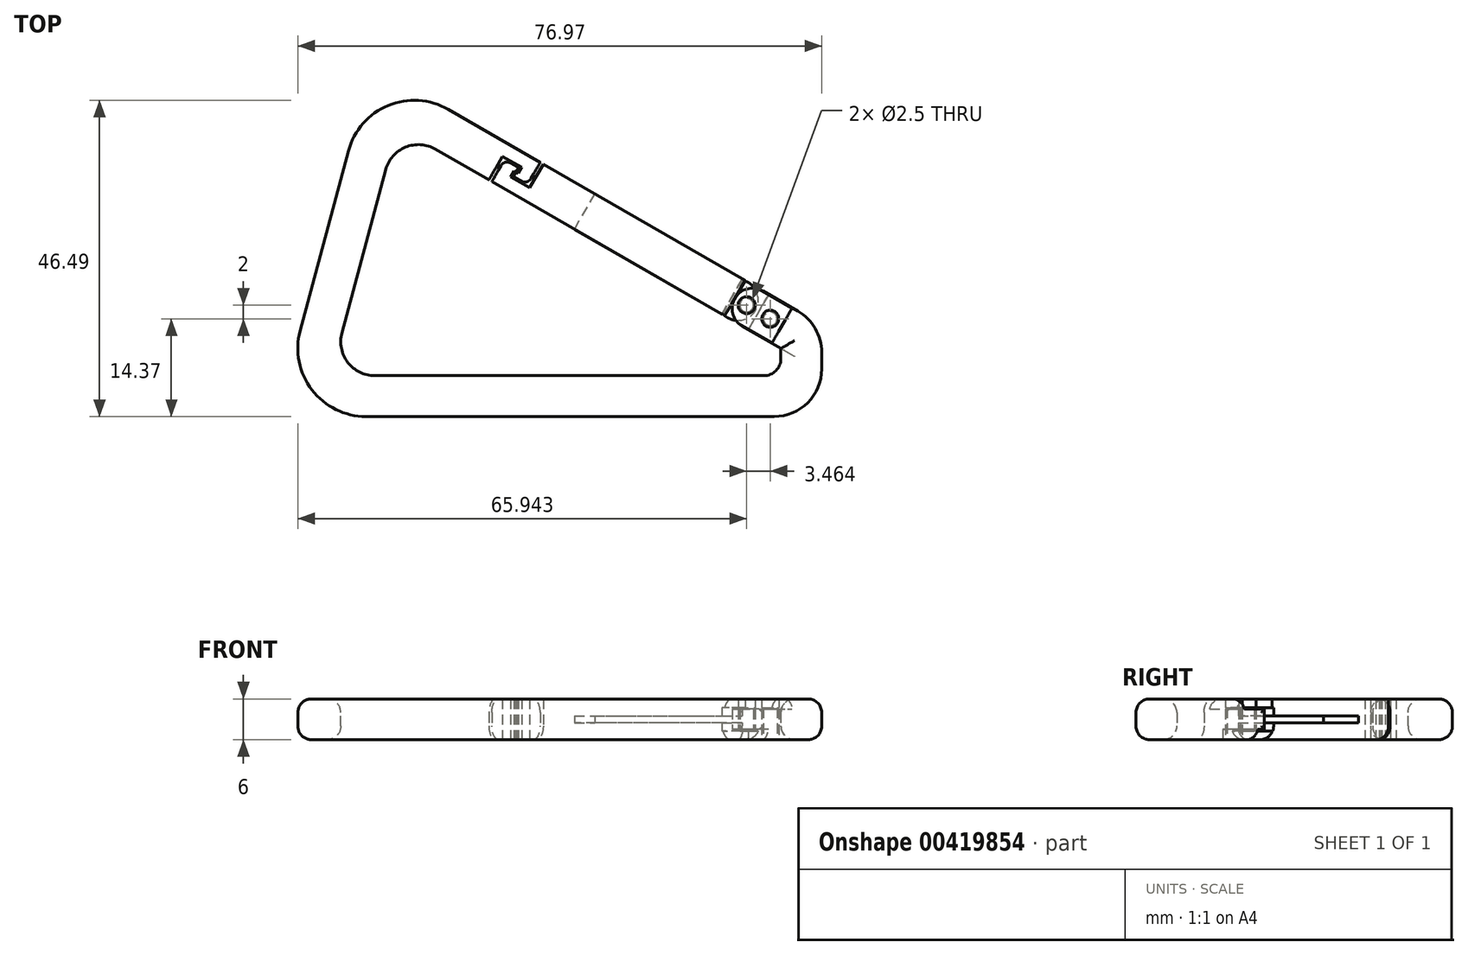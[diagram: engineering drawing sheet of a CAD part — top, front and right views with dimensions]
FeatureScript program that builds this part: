
annotation { "Feature Type Name" : "Feature", "Feature Type Description" : "" }
export const myFeature = defineFeature(function(context is Context, id is Id, definition is map)
    precondition{}
    {
        {
            var Q0;
            Q0=qCreatedBy(makeId("Top.planeOp"),FACE);
            var sketch = newSketch(context, id + "F0", { "sketchPlane" : qUnion([Q0])});
            skLineSegment(sketch, "E0", {"start": v(-46.88, -26.08) * mm, "end": v(33.12, -26.08) * mm});
            skLineSegment(sketch, "E1", {"start": v(33.12, -26.08) * mm, "end": v(33.12, -12.61) * mm});
            skLineSegment(sketch, "E2", {"start": v(33.12, -12.61) * mm, "end": v(21.86, -6.11) * mm});
            skLineSegment(sketch, "E3", {"start": v(-46.88, -26.08) * mm, "end": v(-33.04, 25.58) * mm});
            skLineSegment(sketch, "E4", {"start": v(-33.04, 25.58) * mm, "end": v(-12.78, 13.89) * mm});
            skLineSegment(sketch, "E5", {"start": v(-12.78, 13.89) * mm, "end": v(-15.78, 8.7) * mm});
            skLineSegment(sketch, "E6", {"start": v(-15.78, 8.7) * mm, "end": v(-29.27, 16.48) * mm});
            skLineSegment(sketch, "E7", {"start": v(-29.27, 16.48) * mm, "end": v(-39.06, -20.08) * mm});
            skLineSegment(sketch, "E8", {"start": v(-39.06, -20.08) * mm, "end": v(27.12, -20.08) * mm});
            skLineSegment(sketch, "E9", {"start": v(27.12, -20.08) * mm, "end": v(27.12, -20.08) * mm});
            skLineSegment(sketch, "E10", {"start": v(27.12, -20.08) * mm, "end": v(27.12, -16.08) * mm});
            skLineSegment(sketch, "E11", {"start": v(27.12, -16.08) * mm, "end": v(18.86, -11.3) * mm});
            skLineSegment(sketch, "E12", {"start": v(18.86, -11.3) * mm, "end": v(21.86, -6.11) * mm});
            skLineSegment(sketch, "E13", {"start": v(60.44, -26.08) * mm, "end": v(-63.58, 45.53) * mm, "construction": true});
            skLineSegment(sketch, "E14", {"start": v(-15.95, 15.72) * mm, "end": v(-8.23, 11.26) * mm});
            skLineSegment(sketch, "E15", {"start": v(-8.23, 11.26) * mm, "end": v(-10.1, 8.02) * mm});
            skLineSegment(sketch, "E16", {"start": v(-10.1, 8.02) * mm, "end": v(-11.84, 9.02) * mm});
            skLineSegment(sketch, "E17", {"start": v(-11.84, 9.02) * mm, "end": v(-11.84, 9.02) * mm});
            skLineSegment(sketch, "E18", {"start": v(-11.84, 9.02) * mm, "end": v(-10.97, 10.53) * mm});
            skLineSegment(sketch, "E19", {"start": v(-10.97, 10.53) * mm, "end": v(-13.78, 12.16) * mm});
            skLineSegment(sketch, "E20", {"start": v(-25.7, 17.88) * mm, "end": v(28.11, -13.19) * mm, "construction": true});
            skLineSegment(sketch, "E21", {"start": v(17.25, -10.38) * mm, "end": v(-15.35, 8.44) * mm});
            skLineSegment(sketch, "E22", {"start": v(-15.35, 8.44) * mm, "end": v(-13.47, 11.7) * mm});
            skLineSegment(sketch, "E23", {"start": v(-13.47, 11.7) * mm, "end": v(-13.47, 11.7) * mm});
            skLineSegment(sketch, "E24", {"start": v(-13.47, 11.7) * mm, "end": v(-11.74, 10.7) * mm});
            skLineSegment(sketch, "E25", {"start": v(-11.74, 10.7) * mm, "end": v(-12.62, 9.17) * mm});
            skLineSegment(sketch, "E26", {"start": v(-12.62, 9.17) * mm, "end": v(-9.8, 7.55) * mm});
            skLineSegment(sketch, "E27", {"start": v(-9.8, 7.55) * mm, "end": v(-7.8, 11.01) * mm});
            skLineSegment(sketch, "E28", {"start": v(-7.8, 11.01) * mm, "end": v(21.43, -5.86) * mm});
            skLineSegment(sketch, "E29", {"start": v(21.43, -5.86) * mm, "end": v(18.43, -11.06) * mm});
            skLineSegment(sketch, "E30", {"start": v(18.43, -11.06) * mm, "end": v(17.25, -10.38) * mm});
            skLineSegment(sketch, "E31", {"start": v(25.32, -8.11) * mm, "end": v(22.32, -13.3) * mm});
            skLineSegment(sketch, "E32", {"start": v(25.79, -15.3) * mm, "end": v(28.79, -10.11) * mm});
            skCircle(sketch, "E33", {"center": v(22.1, -9.7) * mm, "radius": 1.25 * mm});
            skCircle(sketch, "E34", {"center": v(25.56, -11.7) * mm, "radius": 1.25 * mm});
            skCircle(sketch, "E35", {"center": v(22.1, -9.7) * mm, "radius": 1 * mm});
            skCircle(sketch, "E36", {"center": v(25.56, -11.7) * mm, "radius": 1 * mm});
            skLineSegment(sketch, "E37", {"start": v(-11.81, 9.87) * mm, "end": v(-11.47, 9.67) * mm});
            skLineSegment(sketch, "E38", {"start": v(-11.74, 10.7) * mm, "end": v(-11.4, 10.5) * mm});
            skLineSegment(sketch, "E39", {"start": v(-11.4, 10.5) * mm, "end": v(-11.77, 9.84) * mm});
            skLineSegment(sketch, "E40", {"start": v(-11.77, 9.84) * mm, "end": v(-12.12, 10.04) * mm});
            skLineSegment(sketch, "E41", {"start": v(-11.84, 9.02) * mm, "end": v(-12.2, 9.22) * mm});
            skLineSegment(sketch, "E42", {"start": v(-12.2, 9.22) * mm, "end": v(-11.81, 9.87) * mm});
            skSolve(sketch);
        }
        {
            var Q0;
            Q0=makeQuery(id+"F0.imprint","IMPRINT",FACE,{"disambiguationData":[TD([[makeQuery(id+"F0.imprint","IMPRINT",EDGE,{"derivedFrom":sQuery(id+"F0.wireOp",EDGE,"E0")}),1.0]])]});
            var Q1;
            {var subQ1=sQuery(id+"F0.wireOp",EDGE,"E15");Q1=makeQuery(id+"F0.imprint","IMPRINT",FACE,{"disambiguationData":[TD([[makeQuery(id+"F0.imprint","IMPRINT",EDGE,{"derivedFrom":subQ1}),-1.0]])]});}
            var Q2;
            {var subQ1=sQuery(id+"F0.wireOp",EDGE,"E31");Q2=makeQuery(id+"F0.imprint","IMPRINT",FACE,{"disambiguationData":[TD([[makeQuery(id+"F0.imprint","IMPRINT",EDGE,{"derivedFrom":subQ1}),1.0]])]});}
            var Q3;
            {var subQ0=sQuery(id+"F0.wireOp",EDGE,"E12");Q3=makeQuery(id+"F0.imprint","IMPRINT",FACE,{"disambiguationData":[TD([[makeQuery(id+"F0.imprint","IMPRINT",EDGE,{"derivedFrom":subQ0}),-1.0]])]});}
            var Q4;
            {var subQ1=sQuery(id+"F0.wireOp",EDGE,"E37");Q4=makeQuery(id+"F0.imprint","IMPRINT",FACE,{"disambiguationData":[TD([[makeQuery(id+"F0.imprint","IMPRINT",EDGE,{"derivedFrom":subQ1}),-1.0]])]});}
            extrude(context, id + "F1", {"entities" : qUnion([Q0, Q1, Q2, Q3, Q4]), "depth" : 6 * mm});
        }
        {
            var Q0;
            Q0=makeQuery(id+"F1.opExtrude","SWEPT_EDGE",EDGE,{"disambiguationData":[OSD([sQuery(id+"F0.wireOp",EDGE,"E3"),sQuery(id+"F0.wireOp",EDGE,"E4")])]});
            var Q1;
            Q1=makeQuery(id+"F1.opExtrude","SWEPT_EDGE",EDGE,{"disambiguationData":[OSD([sQuery(id+"F0.wireOp",EDGE,"E0"),sQuery(id+"F0.wireOp",EDGE,"E3")])]});
            fillet(context, id + "F2", {"entities" : qUnion([Q0, Q1]), "radius" : 10 * mm, "tangentPropagation" : true, "allowEdgeOverflow" : false});
        }
        {
            var Q0;
            Q0=makeQuery(id+"F1.opExtrude","SWEPT_EDGE",EDGE,{"disambiguationData":[OSD([sQuery(id+"F0.wireOp",EDGE,"E0"),sQuery(id+"F0.wireOp",EDGE,"E1")])]});
            var Q1;
            Q1=makeQuery(id+"F1.opExtrude","SWEPT_EDGE",EDGE,{"disambiguationData":[OSD([sQuery(id+"F0.wireOp",EDGE,"E1"),sQuery(id+"F0.wireOp",EDGE,"E2")])]});
            fillet(context, id + "F3", {"entities" : qUnion([Q0, Q1]), "radius" : 7 * mm, "tangentPropagation" : true, "allowEdgeOverflow" : false});
        }
        {
            var Q0;
            Q0=makeQuery(id+"F1.opExtrude","SWEPT_EDGE",EDGE,{"disambiguationData":[OSD([sQuery(id+"F0.wireOp",EDGE,"E8"),sQuery(id+"F0.wireOp",EDGE,"E10")])]});
            fillet(context, id + "F4", {"entities" : qUnion([Q0]), "radius" : 2.5 * mm, "tangentPropagation" : true, "allowEdgeOverflow" : false});
        }
        {
            var Q0;
            Q0=makeQuery(id+"F1.opExtrude","SWEPT_EDGE",EDGE,{"disambiguationData":[OSD([sQuery(id+"F0.wireOp",EDGE,"E6"),sQuery(id+"F0.wireOp",EDGE,"E7")])]});
            var Q1;
            Q1=makeQuery(id+"F1.opExtrude","SWEPT_EDGE",EDGE,{"disambiguationData":[OSD([sQuery(id+"F0.wireOp",EDGE,"E7"),sQuery(id+"F0.wireOp",EDGE,"E8")])]});
            fillet(context, id + "F5", {"entities" : qUnion([Q0, Q1]), "radius" : 5 * mm, "tangentPropagation" : true, "allowEdgeOverflow" : false});
        }
        {
            var Q0;
            {var subQ0=sQuery(id+"F0.wireOp",EDGE,"E12");Q0=makeQuery(id+"F0.imprint","IMPRINT",FACE,{"disambiguationData":[TD([[makeQuery(id+"F0.imprint","IMPRINT",EDGE,{"derivedFrom":subQ0}),-1.0]])]});}
            extrude(context, id + "F6", {"entities" : qUnion([Q0]), "operationType" : NewBodyOperationType.REMOVE, "depth" : 1.5 * mm});
        }
        {
            var Q0;
            Q0=makeQuery(id+"F0.imprint","IMPRINT",FACE,{"disambiguationData":[TD([[makeQuery(id+"F0.imprint","IMPRINT",EDGE,{"derivedFrom":sQuery(id+"F0.wireOp",EDGE,"E21")}),-1.0]])]});
            var Q1;
            {var subQ3=sQuery(id+"F0.wireOp",EDGE,"E38");Q1=makeQuery(id+"F0.imprint","IMPRINT",FACE,{"disambiguationData":[TD([[makeQuery(id+"F0.imprint","IMPRINT",EDGE,{"derivedFrom":subQ3}),-1.0]])]});}
            extrude(context, id + "F7", {"entities" : qUnion([Q0, Q1]), "depth" : 6 * mm});
        }
        {
            var Q0;
            Q0=makeQuery(id+"F7.opExtrude","SWEPT_FACE",FACE,{"disambiguationData":[OSD([sQuery(id+"F0.wireOp",EDGE,"E29")])]});
            var sketch = newSketch(context, id + "F8", { "sketchPlane" : qUnion([Q0])});
            skLineSegment(sketch, "E43", {"start": v(5.64, 6) * mm, "end": v(-0.86, 6) * mm});
            skLineSegment(sketch, "E44", {"start": v(-0.86, 6) * mm, "end": v(-0.86, 0) * mm});
            skLineSegment(sketch, "E45", {"start": v(-0.86, 0) * mm, "end": v(5.64, 0) * mm});
            skLineSegment(sketch, "E46", {"start": v(5.64, 0) * mm, "end": v(5.64, 1.3) * mm});
            skLineSegment(sketch, "E47", {"start": v(5.64, 1.3) * mm, "end": v(-0.36, 1.3) * mm});
            skLineSegment(sketch, "E48", {"start": v(-0.36, 1.3) * mm, "end": v(-0.36, 6) * mm});
            skLineSegment(sketch, "E49", {"start": v(5.64, 6) * mm, "end": v(5.64, 4.7) * mm});
            skLineSegment(sketch, "E50", {"start": v(5.64, 4.7) * mm, "end": v(-0.36, 4.7) * mm});
            skLineSegment(sketch, "E51", {"start": v(-0.36, 4.7) * mm, "end": v(-0.86, 4.7) * mm});
            skLineSegment(sketch, "E52", {"start": v(-0.36, 1.3) * mm, "end": v(-0.86, 1.3) * mm});
            skSolve(sketch);
        }
        {
            var Q0;
            {var subQ0=sQuery(id+"F8.wireOp",EDGE,"E49");Q0=makeQuery(id+"F8.imprint","IMPRINT",FACE,{"disambiguationData":[TD([[makeQuery(id+"F8.imprint","IMPRINT",EDGE,{"derivedFrom":subQ0}),-1.0]])]});}
            extrude(context, id + "F9", {"entities" : qUnion([Q0]), "operationType" : NewBodyOperationType.ADD, "depth" : 8 * mm});
        }
        {
            var Q0;
            {var subQ0=sQuery(id+"F8.wireOp",EDGE,"E46");Q0=makeQuery(id+"F8.imprint","IMPRINT",FACE,{"disambiguationData":[TD([[makeQuery(id+"F8.imprint","IMPRINT",EDGE,{"derivedFrom":subQ0}),-1.0]])]});}
            extrude(context, id + "F10", {"entities" : qUnion([Q0]), "operationType" : NewBodyOperationType.ADD, "depth" : 4 * mm});
        }
        {
            var Q0;
            {var subQ1=sQuery(id+"F0.wireOp",EDGE,"E31");Q0=makeQuery(id+"F0.imprint","IMPRINT",FACE,{"disambiguationData":[TD([[makeQuery(id+"F0.imprint","IMPRINT",EDGE,{"derivedFrom":subQ1}),1.0]])]});}
            var Q1;
            {var subQ0=sQuery(id+"F0.wireOp",EDGE,"E12");Q1=makeQuery(id+"F0.imprint","IMPRINT",FACE,{"disambiguationData":[TD([[makeQuery(id+"F0.imprint","IMPRINT",EDGE,{"derivedFrom":subQ0}),-1.0]])]});}
            extrude(context, id + "F11", {"entities" : qUnion([Q0, Q1]), "operationType" : NewBodyOperationType.REMOVE, "depth" : 6 * mm, "hasSecondDirection" : true, "secondDirectionOppositeDirection" : false, "secondDirectionDepth" : 4.5 * mm});
        }
        {
            var Q0;
            Q0=makeQuery(id+"F0.imprint","IMPRINT",FACE,{"disambiguationData":[TD([[makeQuery(id+"F0.imprint","IMPRINT",EDGE,{"derivedFrom":sQuery(id+"F0.wireOp",EDGE,"E36")}),1.0]])]});
            extrude(context, id + "F12", {"entities" : qUnion([Q0]), "operationType" : NewBodyOperationType.ADD, "depth" : 6 * mm});
        }
        {
            var Q0;
            Q0=makeQuery(id+"F0.imprint","IMPRINT",FACE,{"disambiguationData":[TD([[makeQuery(id+"F0.imprint","IMPRINT",EDGE,{"derivedFrom":sQuery(id+"F0.wireOp",EDGE,"E35")}),1.0]])]});
            var Q1;
            Q1=sQuery(id+"F0.wireOp",EDGE,"E35");
            extrude(context, id + "F13", {"entities" : qUnion([Q0]), "operationType" : NewBodyOperationType.ADD, "surfaceEntities" : qUnion([Q1]), "depth" : 4.5 * mm});
        }
        {
            var Q0;
            Q0=makeQuery(id+"F10.boolean.opBoolean","MERGE",FACE,{"derivedFrom":[makeQuery(id+"F9.boolean.opBoolean","MERGE",FACE,{"derivedFrom":[makeQuery(id+"F7.opExtrude","SWEPT_FACE",FACE,{"disambiguationData":[OSD([sQuery(id+"F0.wireOp",EDGE,"E28")])]}),makeQuery(id+"F9.opExtrude","SWEPT_FACE",FACE,{"disambiguationData":[OSD([sQuery(id+"F8.wireOp",EDGE,"E49")])]})]}),makeQuery(id+"F10.opExtrude","SWEPT_FACE",FACE,{"disambiguationData":[OSD([sQuery(id+"F8.wireOp",EDGE,"E46")])]})]});
            var sketch = newSketch(context, id + "F14", { "sketchPlane" : qUnion([Q0])});
            skLineSegment(sketch, "E53", {"start": v(-21.49, 3) * mm, "end": v(9.93, 3) * mm, "construction": true});
            skLineSegment(sketch, "E54", {"start": v(3.51, 3.5) * mm, "end": v(3.51, 2.5) * mm});
            skLineSegment(sketch, "E55", {"start": v(3.51, 3.5) * mm, "end": v(-21.49, 3.5) * mm});
            skLineSegment(sketch, "E56", {"start": v(-21.49, 3.5) * mm, "end": v(-21.49, 2.5) * mm});
            skLineSegment(sketch, "E57", {"start": v(-21.49, 2.5) * mm, "end": v(3.51, 2.5) * mm});
            skSolve(sketch);
        }
        {
            var Q0;
            Q0 = qSketchRegion(id + "F14", true);
            extrude(context, id + "F15", {"entities" : qUnion([Q0]), "operationType" : NewBodyOperationType.REMOVE, "oppositeDirection" : true, "depth" : 6 * mm});
        }
        {
            var Q0;
            Q0=makeQuery(id+"F1.opExtrude","CAP_EDGE",EDGE,{"disambiguationData":[OSD([sQuery(id+"F0.wireOp",EDGE,"E0")])],"isStart":true});
            var Q1;
            Q1=makeQuery(id+"F1.opExtrude","CAP_EDGE",EDGE,{"disambiguationData":[OSD([sQuery(id+"F0.wireOp",EDGE,"E0")])],"isStart":false});
            var Q2;
            Q2=makeQuery(id+"F1.opExtrude","CAP_EDGE",EDGE,{"disambiguationData":[OSD([sQuery(id+"F0.wireOp",EDGE,"E7")])],"isStart":false});
            var Q3;
            Q3=makeQuery(id+"F1.opExtrude","CAP_EDGE",EDGE,{"disambiguationData":[OSD([sQuery(id+"F0.wireOp",EDGE,"E8")])],"isStart":true});
            fillet(context, id + "F16", {"entities" : qUnion([Q0, Q1, Q2, Q3]), "radius" : 2 * mm, "tangentPropagation" : true, "allowEdgeOverflow" : false});
        }
        {
            var Q0;
            Q0=makeQuery(id+"F9.opExtrude","CAP_EDGE",EDGE,{"disambiguationData":[OSD([sQuery(id+"F8.wireOp",EDGE,"E49")])],"isStart":false});
            var Q1;
            Q1=makeQuery(id+"F9.opExtrude","CAP_EDGE",EDGE,{"disambiguationData":[OSD([sQuery(id+"F8.wireOp",EDGE,"E48")])],"isStart":false});
            var Q2;
            Q2=makeQuery(id+"F10.opExtrude","CAP_EDGE",EDGE,{"disambiguationData":[OSD([sQuery(id+"F8.wireOp",EDGE,"E46")])],"isStart":false});
            var Q3;
            Q3=makeQuery(id+"F10.opExtrude","CAP_EDGE",EDGE,{"disambiguationData":[OSD([sQuery(id+"F0.wireOp",EDGE,"E29"),sQuery(id+"F0.wireOp",EDGE,"E30")])],"isStart":false});
            fillet(context, id + "F17", {"entities" : qUnion([Q0, Q1, Q2, Q3]), "radius" : 3 * mm, "tangentPropagation" : true, "allowEdgeOverflow" : false});
        }
        {
            var Q0;
            Q0=makeQuery(id+"F1.opExtrude","SWEPT_EDGE",EDGE,{"disambiguationData":[OSD([sQuery(id+"F0.wireOp",EDGE,"E11"),sQuery(id+"F0.wireOp",EDGE,"E12")])]});
            var Q1;
            Q1=makeQuery(id+"F1.opExtrude","SWEPT_EDGE",EDGE,{"disambiguationData":[OSD([sQuery(id+"F0.wireOp",EDGE,"E2"),sQuery(id+"F0.wireOp",EDGE,"E12")])]});
            fillet(context, id + "F18", {"entities" : qUnion([Q0, Q1]), "radius" : 3 * mm, "tangentPropagation" : true, "allowEdgeOverflow" : false});
        }
        {
            var Q0;
            Q0=makeQuery(id+"F9.boolean.opBoolean","MERGE",EDGE,{"derivedFrom":[makeQuery(id+"F7.opExtrude","CAP_EDGE",EDGE,{"disambiguationData":[OSD([sQuery(id+"F0.wireOp",EDGE,"E21"),sQuery(id+"F0.wireOp",EDGE,"E30")])],"isStart":false}),makeQuery(id+"F9.opExtrude","SWEPT_EDGE",EDGE,{"disambiguationData":[OSD([sQuery(id+"F8.wireOp",EDGE,"E43"),sQuery(id+"F8.wireOp",EDGE,"E48")])]})]});
            var Q1;
            {var subQ0=sQuery(id+"F0.wireOp",EDGE,"E30");Q1=makeQuery(id+"F10.boolean.opBoolean","MERGE",EDGE,{"derivedFrom":[makeQuery(id+"F7.opExtrude","CAP_EDGE",EDGE,{"disambiguationData":[OSD([sQuery(id+"F0.wireOp",EDGE,"E21"),subQ0])],"isStart":true}),makeQuery(id+"F10.opExtrude","SWEPT_EDGE",EDGE,{"disambiguationData":[OSD([sQuery(id+"F0.wireOp",EDGE,"E29"),subQ0,sQuery(id+"F8.wireOp",EDGE,"E45")])]})]});}
            fillet(context, id + "F19", {"entities" : qUnion([Q0, Q1]), "radius" : 2 * mm, "tangentPropagation" : true, "allowEdgeOverflow" : false});
        }
        {
            var Q0;
            Q0=makeQuery(id+"F1.opExtrude","SWEPT_EDGE",EDGE,{"disambiguationData":[OSD([sQuery(id+"F0.wireOp",EDGE,"E41"),sQuery(id+"F0.wireOp",EDGE,"E42")])]});
            var Q1;
            Q1=makeQuery(id+"F7.opExtrude","SWEPT_EDGE",EDGE,{"disambiguationData":[OSD([sQuery(id+"F0.wireOp",EDGE,"E37"),sQuery(id+"F0.wireOp",EDGE,"E39"),sQuery(id+"F0.wireOp",EDGE,"E40")])]});
            var Q2;
            Q2=makeQuery(id+"F7.opExtrude","SWEPT_EDGE",EDGE,{"disambiguationData":[OSD([sQuery(id+"F0.wireOp",EDGE,"E38"),sQuery(id+"F0.wireOp",EDGE,"E39")])]});
            var Q3;
            Q3=makeQuery(id+"F1.opExtrude","SWEPT_EDGE",EDGE,{"disambiguationData":[OSD([sQuery(id+"F0.wireOp",EDGE,"E40"),sQuery(id+"F0.wireOp",EDGE,"E42")])]});
            fillet(context, id + "F20", {"entities" : qUnion([Q0, Q1, Q2, Q3]), "radius" : .35 * mm, "tangentPropagation" : true, "allowEdgeOverflow" : false});
        }
        {
            var Q0;
            Q0=makeQuery(id+"F1.opExtrude","SWEPT_EDGE",EDGE,{"disambiguationData":[OSD([sQuery(id+"F0.wireOp",EDGE,"E15"),sQuery(id+"F0.wireOp",EDGE,"E16")])]});
            var Q1;
            Q1=makeQuery(id+"F7.opExtrude","SWEPT_EDGE",EDGE,{"disambiguationData":[OSD([sQuery(id+"F0.wireOp",EDGE,"E22"),sQuery(id+"F0.wireOp",EDGE,"E24")])]});
            fillet(context, id + "F21", {"entities" : qUnion([Q0, Q1]), "radius" : 1 * mm, "tangentPropagation" : true, "allowEdgeOverflow" : false});
        }
    });
